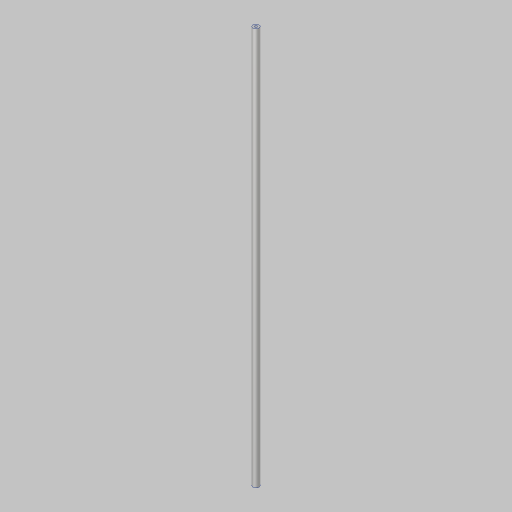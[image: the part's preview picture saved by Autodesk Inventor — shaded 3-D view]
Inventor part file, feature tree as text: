
AUTODESK INVENTOR PART (.ipt)
format: ipt  version: 2023.5 (Build 275446000, 446)  size: 89,600 bytes
history: native  units: in
note: dims shown in document units (in); Inventor stores cm internally (conversion verified against a paired STEP export)
features: sketch x3, hole x2, extrude x1
ambient origin geometry x8: Origin, YZ Plane, XZ Plane, XY Plane, X Axis, Y Axis, Z Axis, Center Point
bodies: Solid1 (feature_tree)
feature tree (6):
  extrude  "Extrusion1"  Depth=32.5in TaperAngle=0.0deg
  hole  "Hole1"  [1 undecoded]
  hole  "Hole2"  [1 undecoded]
  sketch  "Sketch1"  dims[d0=0.5in d1=32.5in d2=0.0in]
  sketch  "Sketch2"  dims[d3=0.196in d4=0.5in d5=0.507in d6=0.25in d7=0.5635in d8=0.75in d9=0.8108in]
  sketch  "Sketch3"  dims[d10=0.196in d11=0.5in d12=0.375in d13=0.25in d14=0.5635in d15=1.5in d16=0.8108in]
note: 2 required parameter values undecoded (feature->parameter linkage not recoverable at this tier; creation-order binding heuristic only, values carry confidence <= 0.55)
